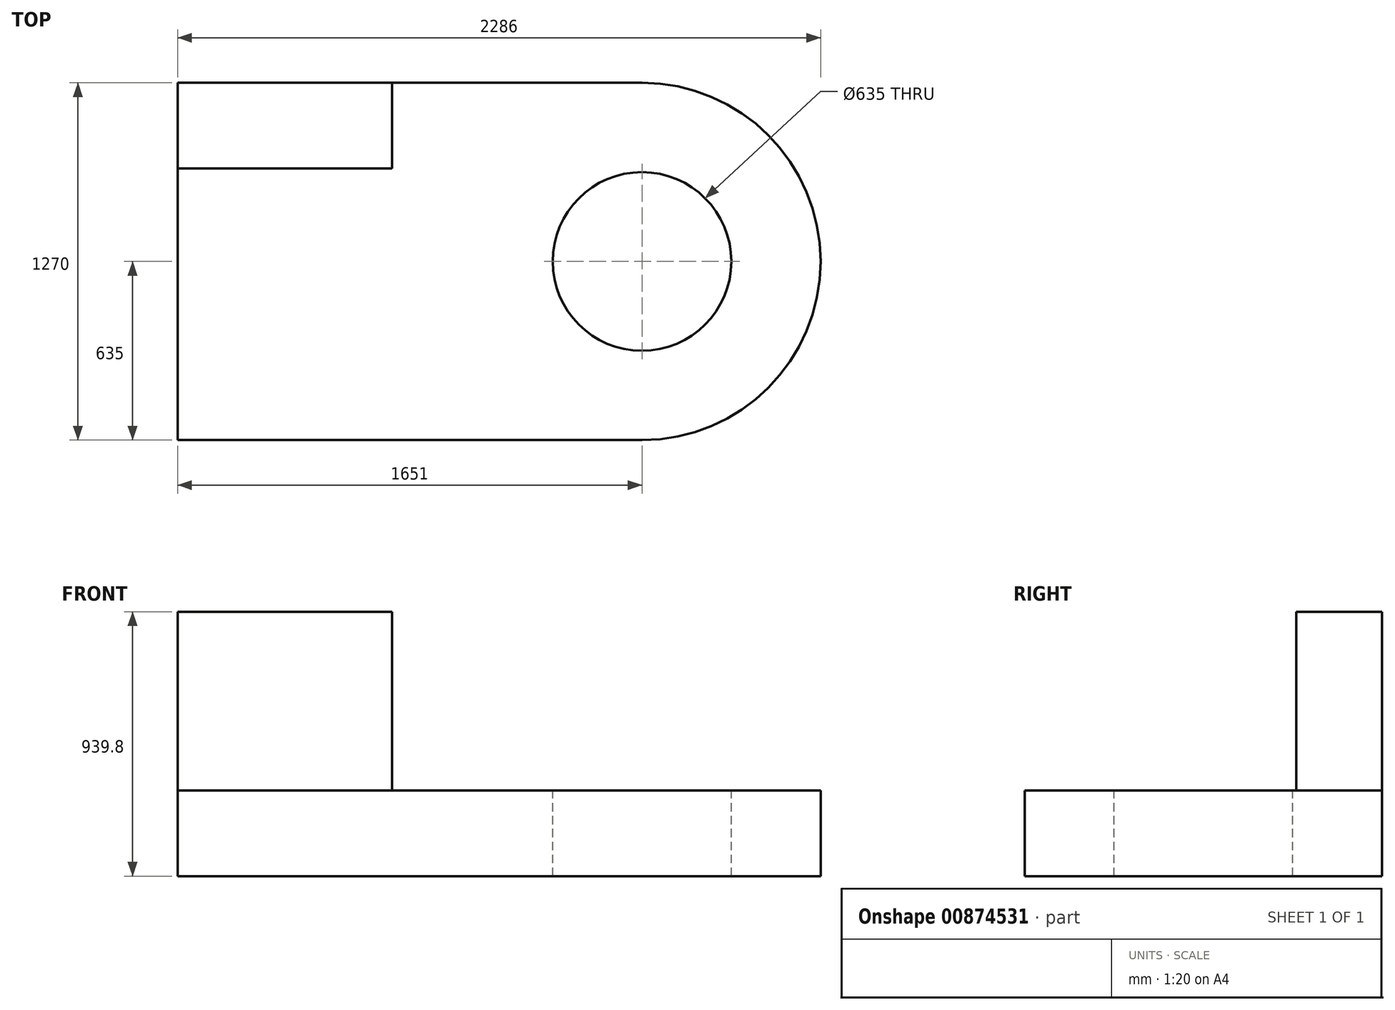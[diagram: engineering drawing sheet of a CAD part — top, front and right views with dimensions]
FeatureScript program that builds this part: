
annotation { "Feature Type Name" : "Feature", "Feature Type Description" : "" }
export const myFeature = defineFeature(function(context is Context, id is Id, definition is map)
    precondition{}
    {
        {
            var Q0;
            Q0=qCreatedBy(makeId("Front.planeOp"),FACE);
            var sketch = newSketch(context, id + "F0", { "sketchPlane" : qUnion([Q0])});
            skLineSegment(sketch, "E0.bottom", {"start": v(0, 0) * mm, "end": v(-762, 0) * mm});
            skLineSegment(sketch, "E0.top", {"start": v(0, 939.8) * mm, "end": v(-762, 939.8) * mm});
            skLineSegment(sketch, "E0.left", {"start": v(0, 0) * mm, "end": v(0, 939.8) * mm});
            skLineSegment(sketch, "E0.right", {"start": v(-762, 0) * mm, "end": v(-762, 939.8) * mm});
            skSolve(sketch);
        }
        {
            var Q0;
            Q0=makeQuery(id+"F0.imprint","IMPRINT",FACE,{"disambiguationData":[TD([[makeQuery(id+"F0.imprint","IMPRINT",EDGE,{"derivedFrom":sQuery(id+"F0.wireOp",EDGE,"E0.bottom")}),-1.0]])]});
            extrude(context, id + "F1", {"entities" : qUnion([Q0]), "depth" : 304.8 * mm, "offsetDistance" : 25.4 * mm});
        }
        {
            var Q0;
            Q0=makeQuery(id+"F1.opExtrude","CAP_FACE",FACE,{"disambiguationData":[OSD([sQuery(id+"F0.wireOp",EDGE,"E0.bottom"),sQuery(id+"F0.wireOp",EDGE,"E0.top"),sQuery(id+"F0.wireOp",EDGE,"E0.left"),sQuery(id+"F0.wireOp",EDGE,"E0.right")])],"isStart":false});
            var sketch = newSketch(context, id + "F2", { "sketchPlane" : qUnion([Q0])});
            skLineSegment(sketch, "E1", {"start": v(-762, 0) * mm, "end": v(-762, 304.8) * mm});
            skLineSegment(sketch, "E2", {"start": v(-762, 304.8) * mm, "end": v(0, 304.8) * mm});
            skSolve(sketch);
        }
        {
            var Q0;
            Q0=makeQuery(id+"F2.imprint","IMPRINT",FACE,{"disambiguationData":[TD([[makeQuery(id+"F2.imprint","IMPRINT",EDGE,{"derivedFrom":sQuery(id+"F2.wireOp",EDGE,"E1")}),-1.0]])]});
            extrude(context, id + "F3", {"entities" : qUnion([Q0]), "operationType" : NewBodyOperationType.ADD, "depth" : 965.2 * mm, "offsetDistance" : 25.4 * mm});
        }
        {
            var Q0;
            {var subQ0=sQuery(id+"F0.wireOp",EDGE,"E0.left");Q0=makeQuery(id+"F3.boolean.opBoolean","MERGE",FACE,{"derivedFrom":[makeQuery(id+"F1.opExtrude","SWEPT_FACE",FACE,{"disambiguationData":[OSD([subQ0])]}),makeQuery(id+"F3.opExtrude","SWEPT_FACE",FACE,{"disambiguationData":[OSD([subQ0])]})]});}
            var sketch = newSketch(context, id + "F4", { "sketchPlane" : qUnion([Q0])});
            skLineSegment(sketch, "E3", {"start": v(-304.8, 304.8) * mm, "end": v(0, 304.8) * mm});
            skSolve(sketch);
        }
        {
            var Q0;
            {var subQ3=sQuery(id+"F4.wireOp",EDGE,"E3");Q0=makeQuery(id+"F4.imprint","IMPRINT",FACE,{"disambiguationData":[TD([[makeQuery(id+"F4.imprint","IMPRINT",EDGE,{"derivedFrom":subQ3}),-1.0]])]});}
            extrude(context, id + "F5", {"entities" : qUnion([Q0]), "operationType" : NewBodyOperationType.ADD, "depth" : 889 * mm, "offsetDistance" : 25.4 * mm});
        }
        {
            var Q0;
            {var subQ0=sQuery(id+"F2.wireOp",EDGE,"E2");Q0=makeQuery(id+"F5.boolean.opBoolean","MERGE",FACE,{"derivedFrom":[makeQuery(id+"F3.opExtrude","SWEPT_FACE",FACE,{"disambiguationData":[OSD([subQ0])]}),makeQuery(id+"F5.opExtrude","SWEPT_FACE",FACE,{"disambiguationData":[OSD([sQuery(id+"F0.wireOp",EDGE,"E0.left"),subQ0,sQuery(id+"F4.wireOp",EDGE,"E3")])]})]});}
            var sketch = newSketch(context, id + "F6", { "sketchPlane" : qUnion([Q0])});
            skCircle(sketch, "E4", {"center": v(889, -635) * mm, "radius": 635 * mm});
            skSolve(sketch);
        }
        {
            var Q0;
            {var subQ1=sQuery(id+"F2.wireOp",EDGE,"E2");var subQ2=sQuery(id+"F0.wireOp",EDGE,"E0.left");var subQ3=sQuery(id+"F4.wireOp",EDGE,"E3");var subQ4=makeQuery(id+"F5.opExtrude","CAP_EDGE",EDGE,{"disambiguationData":[OSD([subQ2,subQ1,subQ3])],"isStart":false});Q0=makeQuery(id+"F6.imprint","IMPRINT",FACE,{"disambiguationData":[TD([[makeQuery(id+"F6.imprint","IMPRINT",EDGE,{"derivedFrom":subQ4}),-1.0]])]});}
            extrude(context, id + "F7", {"entities" : qUnion([Q0]), "operationType" : NewBodyOperationType.ADD, "oppositeDirection" : true, "depth" : 304.8 * mm, "offsetDistance" : 25.4 * mm});
        }
        {
            var Q0;
            {var subQ0=sQuery(id+"F4.wireOp",EDGE,"E3");var subQ1=sQuery(id+"F2.wireOp",EDGE,"E2");var subQ2=sQuery(id+"F0.wireOp",EDGE,"E0.left");Q0=makeQuery(id+"F7.boolean.opBoolean","MERGE",FACE,{"derivedFrom":[makeQuery(id+"F5.boolean.opBoolean","MERGE",FACE,{"derivedFrom":[makeQuery(id+"F3.opExtrude","SWEPT_FACE",FACE,{"disambiguationData":[OSD([subQ1])]}),makeQuery(id+"F5.opExtrude","SWEPT_FACE",FACE,{"disambiguationData":[OSD([subQ2,subQ1,subQ0])]})]}),makeQuery(id+"F7.opExtrude","CAP_FACE",FACE,{"disambiguationData":[OSD([subQ2,subQ1,subQ0,sQuery(id+"F6.wireOp",EDGE,"E4")])],"isStart":true})]});}
            var sketch = newSketch(context, id + "F8", { "sketchPlane" : qUnion([Q0])});
            skCircle(sketch, "E5", {"center": v(889, -635) * mm, "radius": 317.5 * mm});
            skSolve(sketch);
        }
        {
            var Q0;
            Q0=makeQuery(id+"F8.imprint","IMPRINT",FACE,{"disambiguationData":[TD([[makeQuery(id+"F8.imprint","IMPRINT",EDGE,{"derivedFrom":sQuery(id+"F8.wireOp",EDGE,"E5")}),1.0]])]});
            extrude(context, id + "F9", {"entities" : qUnion([Q0]), "operationType" : NewBodyOperationType.REMOVE, "oppositeDirection" : true, "depth" : 15240 * mm, "offsetDistance" : 25.4 * mm});
        }
    });
